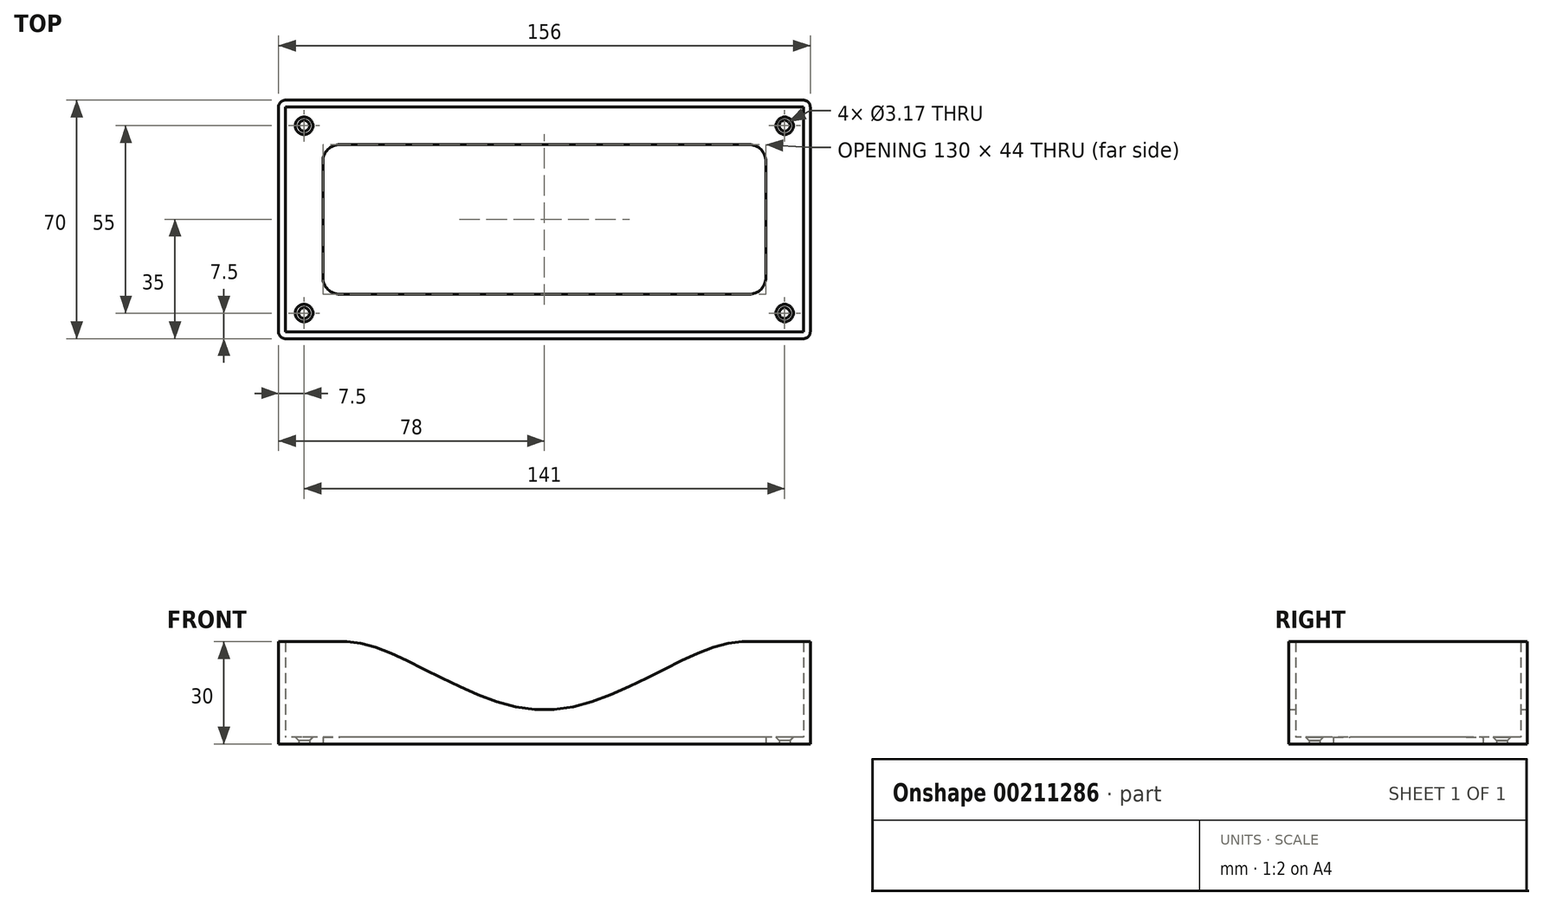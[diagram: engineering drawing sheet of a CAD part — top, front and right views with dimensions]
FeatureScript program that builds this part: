
annotation { "Feature Type Name" : "Feature", "Feature Type Description" : "" }
export const myFeature = defineFeature(function(context is Context, id is Id, definition is map)
    precondition{}
    {
        {
            assignVariable(context, id + "F0", {"name" : "thickness", "anyValue" : 2});
        }
        {
            var Q0;
            Q0=qCreatedBy(makeId("Top.planeOp"),FACE);
            var sketch = newSketch(context, id + "F1", { "sketchPlane" : qUnion([Q0])});
            skLineSegment(sketch, "E0.bottom", {"start": v(75, 32) * mm, "end": v(-75, 32) * mm, "construction": true});
            skLineSegment(sketch, "E0.top", {"start": v(75, -32) * mm, "end": v(-75, -32) * mm, "construction": true});
            skLineSegment(sketch, "E0.left", {"start": v(75, 32) * mm, "end": v(75, -32) * mm, "construction": true});
            skLineSegment(sketch, "E0.right", {"start": v(-75, 32) * mm, "end": v(-75, -32) * mm, "construction": true});
            skPoint(sketch, "E0.middle", {"position": v(0, 0) * mm});
            skLineSegment(sketch, "E1.bottom", {"start": v(76, 33) * mm, "end": v(-76, 33) * mm});
            skLineSegment(sketch, "E1.top", {"start": v(76, -33) * mm, "end": v(-76, -33) * mm});
            skLineSegment(sketch, "E1.left", {"start": v(76, 33) * mm, "end": v(76, -33) * mm});
            skLineSegment(sketch, "E1.right", {"start": v(-76, 33) * mm, "end": v(-76, -33) * mm});
            skLineSegment(sketch, "E2.bottom", {"start": v(76, 35) * mm, "end": v(-76, 35) * mm});
            skLineSegment(sketch, "E2.top", {"start": v(76, -35) * mm, "end": v(-76, -35) * mm});
            skLineSegment(sketch, "E2.left", {"start": v(78, 33) * mm, "end": v(78, -33) * mm});
            skLineSegment(sketch, "E2.right", {"start": v(-78, 33) * mm, "end": v(-78, -33) * mm});
            skPoint(sketch, "E3.visualSharp", {"position": v(-78, 35) * mm});
            skArc(sketch, "E3.filletArc", {"start": v(-76, 35) * mm, "mid": v(-77.41, 34.41) * mm, "end": v(-78, 33) * mm});
            skPoint(sketch, "E4.visualSharp", {"position": v(78, 35) * mm});
            skArc(sketch, "E4.filletArc", {"start": v(78, 33) * mm, "mid": v(77.41, 34.41) * mm, "end": v(76, 35) * mm});
            skPoint(sketch, "E5.visualSharp", {"position": v(78, -35) * mm});
            skArc(sketch, "E5.filletArc", {"start": v(76, -35) * mm, "mid": v(77.41, -34.41) * mm, "end": v(78, -33) * mm});
            skPoint(sketch, "E6.visualSharp", {"position": v(-78, -35) * mm});
            skArc(sketch, "E6.filletArc", {"start": v(-78, -33) * mm, "mid": v(-77.41, -34.41) * mm, "end": v(-76, -35) * mm});
            skLineSegment(sketch, "E7.bottom", {"start": v(60, 22) * mm, "end": v(-60, 22) * mm});
            skLineSegment(sketch, "E7.top", {"start": v(60, -22) * mm, "end": v(-60, -22) * mm});
            skLineSegment(sketch, "E7.left", {"start": v(65, 17) * mm, "end": v(65, -17) * mm});
            skLineSegment(sketch, "E7.right", {"start": v(-65, 17) * mm, "end": v(-65, -17) * mm});
            skPoint(sketch, "E8.visualSharp", {"position": v(-65, 22) * mm});
            skArc(sketch, "E8.filletArc", {"start": v(-60, 22) * mm, "mid": v(-63.54, 20.54) * mm, "end": v(-65, 17) * mm});
            skPoint(sketch, "E9.visualSharp", {"position": v(65, 22) * mm});
            skArc(sketch, "E9.filletArc", {"start": v(65, 17) * mm, "mid": v(63.54, 20.54) * mm, "end": v(60, 22) * mm});
            skPoint(sketch, "E10.visualSharp", {"position": v(65, -22) * mm});
            skArc(sketch, "E10.filletArc", {"start": v(60, -22) * mm, "mid": v(63.54, -20.54) * mm, "end": v(65, -17) * mm});
            skPoint(sketch, "E11.visualSharp", {"position": v(-65, -22) * mm});
            skArc(sketch, "E11.filletArc", {"start": v(-65, -17) * mm, "mid": v(-63.54, -20.54) * mm, "end": v(-60, -22) * mm});
            skLineSegment(sketch, "E12", {"start": v(-76, -33) * mm, "end": v(-65, -22) * mm, "construction": true});
            skLineSegment(sketch, "E13", {"start": v(-76, 33) * mm, "end": v(-65, 22) * mm, "construction": true});
            skLineSegment(sketch, "E14", {"start": v(76, 33) * mm, "end": v(65, 22) * mm, "construction": true});
            skLineSegment(sketch, "E15", {"start": v(76, -33) * mm, "end": v(65, -22) * mm, "construction": true});
            skCircle(sketch, "E16", {"center": v(-70.5, 27.5) * mm, "radius": 1.59 * mm});
            skCircle(sketch, "E17", {"center": v(-70.5, -27.5) * mm, "radius": 1.59 * mm});
            skCircle(sketch, "E18", {"center": v(70.5, 27.5) * mm, "radius": 1.59 * mm});
            skCircle(sketch, "E19", {"center": v(70.5, -27.5) * mm, "radius": 1.59 * mm});
            skSolve(sketch);
        }
        {
            var Q0;
            Q0=makeQuery(id+"F1.imprint","IMPRINT",FACE,{"disambiguationData":[TD([[makeQuery(id+"F1.imprint","IMPRINT",EDGE,{"derivedFrom":sQuery(id+"F1.wireOp",EDGE,"E1.bottom")}),-1.0]])]});
            extrude(context, id + "F2", {"entities" : qUnion([Q0]), "depth" : 30 * mm});
        }
        {
            var Q0;
            Q0 = qSketchRegion(id + "F1", true);
            var Q1;
            Q1=makeQuery(id+"F1.imprint","IMPRINT",FACE,{"disambiguationData":[TD([[makeQuery(id+"F1.imprint","IMPRINT",EDGE,{"derivedFrom":sQuery(id+"F1.wireOp",EDGE,"E1.bottom")}),1.0]])]});
            var Q2;
            Q2=sQuery(id+"F1.wireOp",EDGE,"E0.bottom");
            var Q3;
            Q3=sQuery(id+"F1.wireOp",EDGE,"E0.right");
            var Q4;
            Q4=sQuery(id+"F1.wireOp",EDGE,"E0.top");
            var Q5;
            Q5=sQuery(id+"F1.wireOp",EDGE,"E0.left");
            extrude(context, id + "F3", {"entities" : qUnion([Q0, Q1]), "operationType" : NewBodyOperationType.ADD, "surfaceEntities" : qUnion([Q2, Q3, Q4, Q5]), "depth" : (getVariable(context, 'thickness')) * mm});
        }
        {
            var Q0;
            Q0=makeQuery(id+"F3.opExtrude","CAP_EDGE",EDGE,{"disambiguationData":[OSD([sQuery(id+"F1.wireOp",EDGE,"E16")])],"isStart":false});
            var Q1;
            Q1=makeQuery(id+"F3.opExtrude","CAP_EDGE",EDGE,{"disambiguationData":[OSD([sQuery(id+"F1.wireOp",EDGE,"E18")])],"isStart":false});
            var Q2;
            Q2=makeQuery(id+"F3.opExtrude","CAP_EDGE",EDGE,{"disambiguationData":[OSD([sQuery(id+"F1.wireOp",EDGE,"E19")])],"isStart":false});
            var Q3;
            Q3=makeQuery(id+"F3.opExtrude","CAP_EDGE",EDGE,{"disambiguationData":[OSD([sQuery(id+"F1.wireOp",EDGE,"E17")])],"isStart":false});
            chamfer(context, id + "F4", {"entities" : qUnion([Q0, Q1, Q2, Q3]), "width" : 1 * mm, "tangentPropagation" : true});
        }
        {
            var Q0;
            Q0=qCreatedBy(makeId("Front.planeOp"),FACE);
            var sketch = newSketch(context, id + "F5", { "sketchPlane" : qUnion([Q0])});
            skLineSegment(sketch, "E20.bottom", {"start": v(78, 0) * mm, "end": v(-78, 0) * mm});
            skLineSegment(sketch, "E20.top", {"start": v(78, 30) * mm, "end": v(-78, 30) * mm});
            skLineSegment(sketch, "E20.left", {"start": v(78, 0) * mm, "end": v(78, 30) * mm});
            skLineSegment(sketch, "E20.right", {"start": v(-78, 0) * mm, "end": v(-78, 30) * mm});
            skPoint(sketch, "E20.middle", {"position": v(0, 15) * mm});
            skFitSpline(sketch, "E21", {"points": [v(-58, 30) * mm, v(0, 10) * mm, v(58, 30) * mm], "startDerivative": vector(90, 0) * mm, "endDerivative": vector(90, 0) * mm});
            skSolve(sketch);
        }
        {
            var Q0;
            {var subQ0=sQuery(id+"F5.wireOp",EDGE,"E21");Q0=makeQuery(id+"F5.imprint","IMPRINT",FACE,{"disambiguationData":[TD([[makeQuery(id+"F5.imprint","IMPRINT",EDGE,{"derivedFrom":subQ0}),1.0]])]});}
            var Q1;
            Q1=makeQuery(id+"F2.opExtrude","SWEPT_FACE",FACE,{"disambiguationData":[OSD([sQuery(id+"F1.wireOp",EDGE,"E2.bottom")])]});
            var Q2;
            Q2=makeQuery(id+"F2.opExtrude","SWEPT_FACE",FACE,{"disambiguationData":[OSD([sQuery(id+"F1.wireOp",EDGE,"E2.top")])]});
            extrude(context, id + "F6", {"entities" : qUnion([Q0]), "operationType" : NewBodyOperationType.REMOVE, "endBound" : BoundingType.UP_TO_SURFACE, "oppositeDirection" : true, "endBoundEntityFace" : qUnion([Q1]), "depth" : 25 * mm, "hasSecondDirection" : true, "secondDirectionBound" : SecondDirectionBoundingType.UP_TO_SURFACE, "secondDirectionOppositeDirection" : false, "secondDirectionBoundEntityFace" : qUnion([Q2]), "secondDirectionDepth" : 25 * mm});
        }
    });
